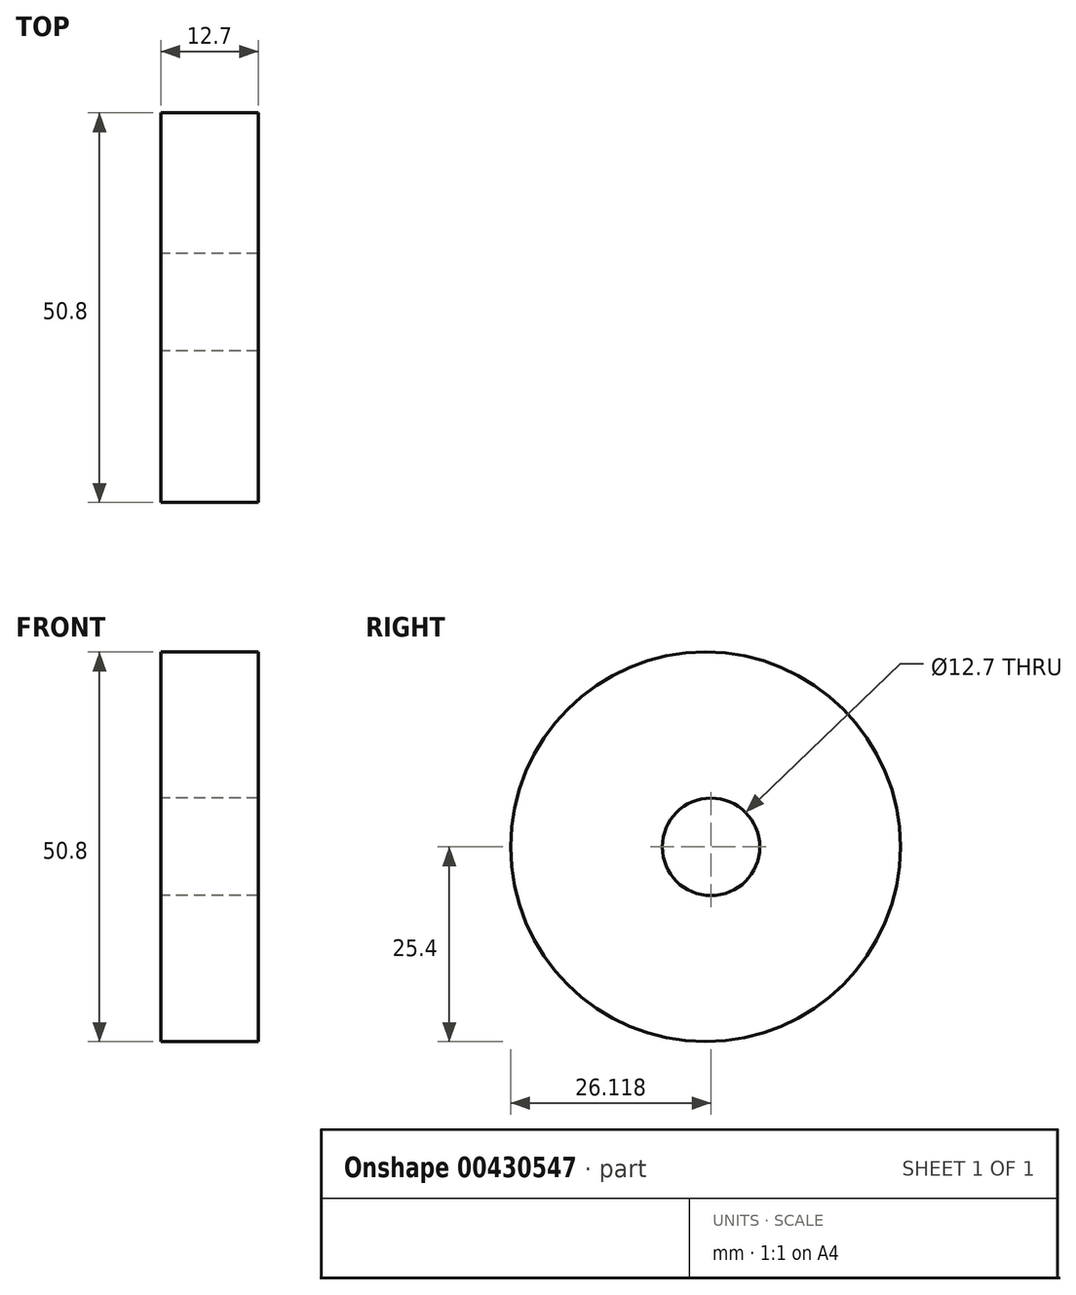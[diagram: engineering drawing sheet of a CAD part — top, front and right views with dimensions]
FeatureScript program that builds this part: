
annotation { "Feature Type Name" : "Feature", "Feature Type Description" : "" }
export const myFeature = defineFeature(function(context is Context, id is Id, definition is map)
    precondition{}
    {
        {
            var Q0;
            Q0=qCreatedBy(makeId("Right.planeOp"),FACE);
            var sketch = newSketch(context, id + "F0", { "sketchPlane" : qUnion([Q0])});
            skCircle(sketch, "E0", {"center": v(0, 0) * mm, "radius": 25.4 * mm});
            skCircle(sketch, "E1", {"center": v(0.72, 0) * mm, "radius": 6.35 * mm});
            skSolve(sketch);
        }
        {
            var Q0;
            Q0=makeQuery(id+"F0.imprint","IMPRINT",FACE,{"disambiguationData":[TD([[makeQuery(id+"F0.imprint","IMPRINT",EDGE,{"derivedFrom":sQuery(id+"F0.wireOp",EDGE,"E0")}),1.0]])]});
            extrude(context, id + "F1", {"entities" : qUnion([Q0]), "depth" : 12.7 * mm});
        }
    });
